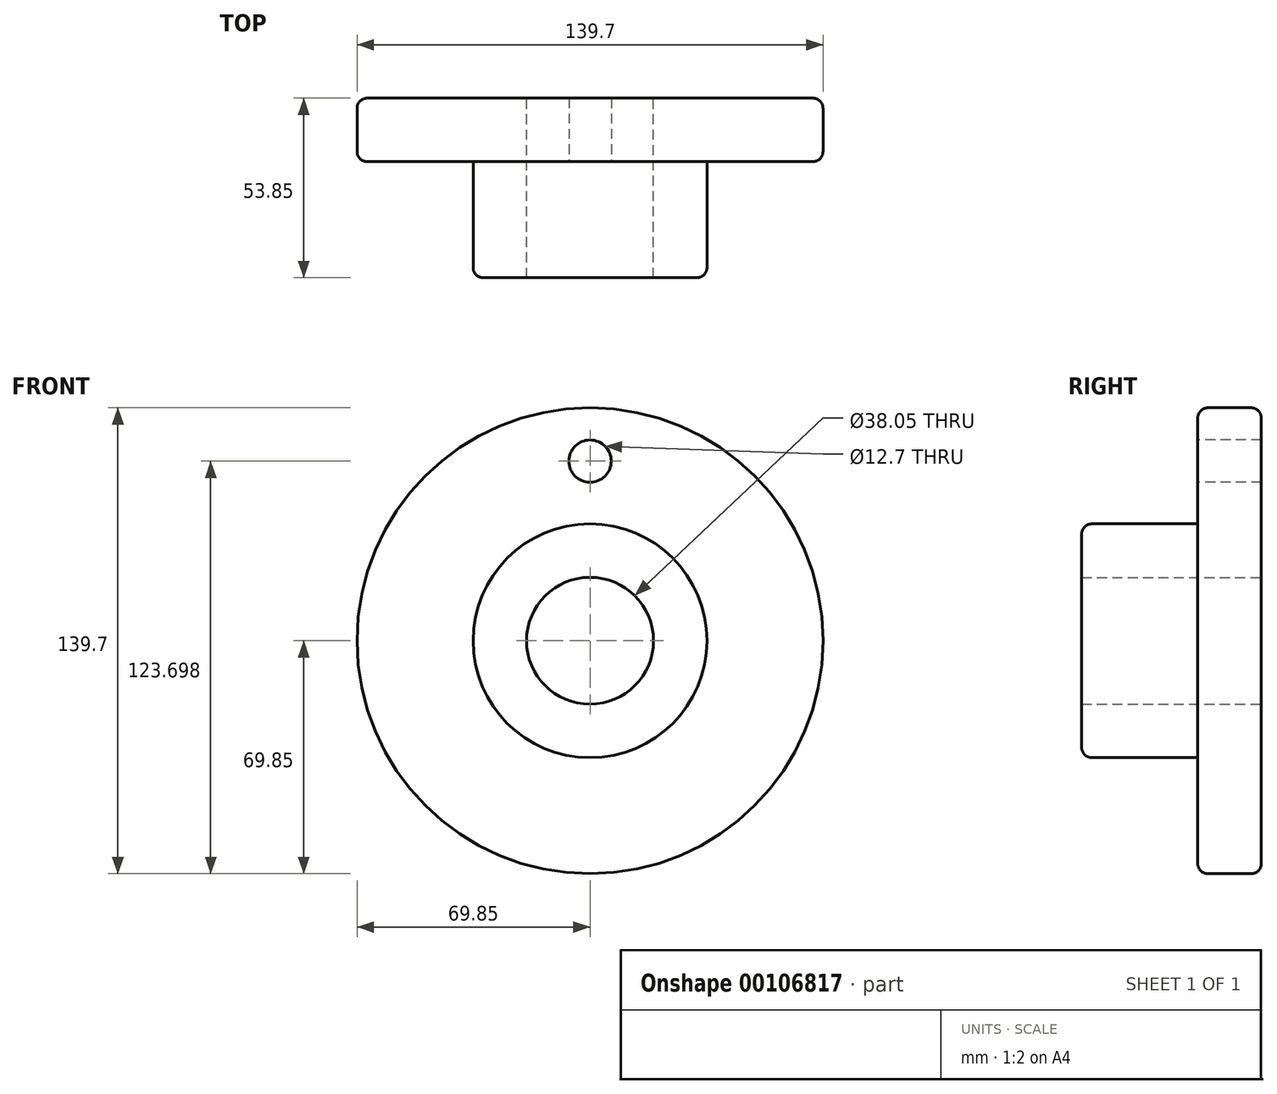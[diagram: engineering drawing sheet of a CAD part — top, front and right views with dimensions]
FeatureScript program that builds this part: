
annotation { "Feature Type Name" : "Feature", "Feature Type Description" : "" }
export const myFeature = defineFeature(function(context is Context, id is Id, definition is map)
    precondition{}
    {
        {
            var Q0;
            Q0=qCreatedBy(makeId("Front.planeOp"),FACE);
            var sketch = newSketch(context, id + "F0", { "sketchPlane" : qUnion([Q0])});
            skCircle(sketch, "E0", {"center": v(0, 0) * mm, "radius": 19.02 * mm});
            skCircle(sketch, "E1", {"center": v(0, 0) * mm, "radius": 35.05 * mm});
            skCircle(sketch, "E2", {"center": v(0, 0) * mm, "radius": 69.85 * mm});
            skCircle(sketch, "E3", {"center": v(0, 0) * mm, "radius": 53.85 * mm});
            skSolve(sketch);
        }
        {
            var Q0;
            Q0=makeQuery(id+"F0.imprint","IMPRINT",FACE,{"disambiguationData":[TD([[makeQuery(id+"F0.imprint","IMPRINT",EDGE,{"derivedFrom":sQuery(id+"F0.wireOp",EDGE,"E0")}),-1.0]])]});
            extrude(context, id + "F1", {"entities" : qUnion([Q0]), "depth" : 53.85 * mm});
        }
        {
            var Q0;
            Q0=makeQuery(id+"F0.imprint","IMPRINT",FACE,{"disambiguationData":[TD([[makeQuery(id+"F0.imprint","IMPRINT",EDGE,{"derivedFrom":sQuery(id+"F0.wireOp",EDGE,"E2")}),1.0]])]});
            var Q1;
            Q1=makeQuery(id+"F0.imprint","IMPRINT",FACE,{"disambiguationData":[TD([[makeQuery(id+"F0.imprint","IMPRINT",EDGE,{"derivedFrom":sQuery(id+"F0.wireOp",EDGE,"E1")}),-1.0]])]});
            extrude(context, id + "F2", {"entities" : qUnion([Q0, Q1]), "operationType" : NewBodyOperationType.ADD, "depth" : 19.05 * mm});
        }
        {
            var Q0;
            Q0=makeQuery(id+"F2.opExtrude","CAP_EDGE",EDGE,{"disambiguationData":[OSD([sQuery(id+"F0.wireOp",EDGE,"E2")])],"isStart":false});
            var Q1;
            Q1=makeQuery(id+"F2.opExtrude","CAP_EDGE",EDGE,{"disambiguationData":[OSD([sQuery(id+"F0.wireOp",EDGE,"E2")])],"isStart":true});
            var Q2;
            Q2=makeQuery(id+"F2.opExtrude","CAP_EDGE",EDGE,{"disambiguationData":[OSD([sQuery(id+"F0.wireOp",EDGE,"E1")])],"isStart":false});
            var Q3;
            Q3=makeQuery(id+"F1.opExtrude","CAP_EDGE",EDGE,{"disambiguationData":[OSD([sQuery(id+"F0.wireOp",EDGE,"E1")])],"isStart":false});
            fillet(context, id + "F3", {"entities" : qUnion([Q0, Q1, Q2, Q3]), "radius" : 3.05 * mm, "tangentPropagation" : true, "allowEdgeOverflow" : false});
        }
        {
            var Q0;
            Q0=makeQuery(id+"F2.opExtrude","CAP_FACE",FACE,{"disambiguationData":[OSD([sQuery(id+"F0.wireOp",EDGE,"E1"),sQuery(id+"F0.wireOp",EDGE,"E2")])],"isStart":false});
            var sketch = newSketch(context, id + "F4", { "sketchPlane" : qUnion([Q0])});
            skCircle(sketch, "E4", {"center": v(0, 53.85) * mm, "radius": 6.35 * mm});
            skSolve(sketch);
        }
        {
            var Q0;
            Q0 = qSketchRegion(id + "F4", true);
            var Q1;
            Q1=makeQuery(id+"FsxHwSPCuyUO7VT_1.1.F4.imprint","IMPRINT",FACE,{"disambiguationData":[TD([[makeQuery(id+"FsxHwSPCuyUO7VT_1.1.F4.imprint","IMPRINT",EDGE,{"derivedFrom":sQuery(id+"FsxHwSPCuyUO7VT_1.1.F4.wireOp",EDGE,"E4")}),1.0]])]});
            var Q2;
            Q2=makeQuery(id+"FsxHwSPCuyUO7VT_1.2.F4.imprint","IMPRINT",FACE,{"disambiguationData":[TD([[makeQuery(id+"FsxHwSPCuyUO7VT_1.2.F4.imprint","IMPRINT",EDGE,{"derivedFrom":sQuery(id+"FsxHwSPCuyUO7VT_1.2.F4.wireOp",EDGE,"E4")}),1.0]])]});
            var Q3;
            Q3=makeQuery(id+"FsxHwSPCuyUO7VT_1.3.F4.imprint","IMPRINT",FACE,{"disambiguationData":[TD([[makeQuery(id+"FsxHwSPCuyUO7VT_1.3.F4.imprint","IMPRINT",EDGE,{"derivedFrom":sQuery(id+"FsxHwSPCuyUO7VT_1.3.F4.wireOp",EDGE,"E4")}),1.0]])]});
            extrude(context, id + "F5", {"entities" : qUnion([Q0, Q1, Q2, Q3]), "operationType" : NewBodyOperationType.REMOVE, "endBound" : BoundingType.THROUGH_ALL, "oppositeDirection" : true, "depth" : 25.4 * mm});
        }
    });
